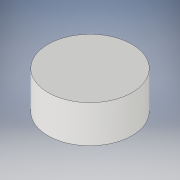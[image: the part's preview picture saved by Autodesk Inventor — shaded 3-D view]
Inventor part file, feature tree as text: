
AUTODESK INVENTOR PART (.ipt)
format: ipt  version: 2018.2 (Build 222227000, 227)  size: 96,256 bytes
history: native  units: in
note: dims shown in document units (in); Inventor stores cm internally (conversion verified against a paired STEP export)
features: sketch x3, extrude x1
ambient origin geometry x8: Origin, YZ Plane, XZ Plane, XY Plane, X Axis, Y Axis, Z Axis, Center Point
bodies: Solid1 (feature_tree)
feature tree (4):
  sketch  "Sketch1"  dims[d0=3.4449in d1=1.5354in d2=0.0in]
  sketch  "3D Sketch1"
  extrude  "Extrusion1"  Depth=1.5354in TaperAngle=0.0deg
  sketch  "Sketch2"
